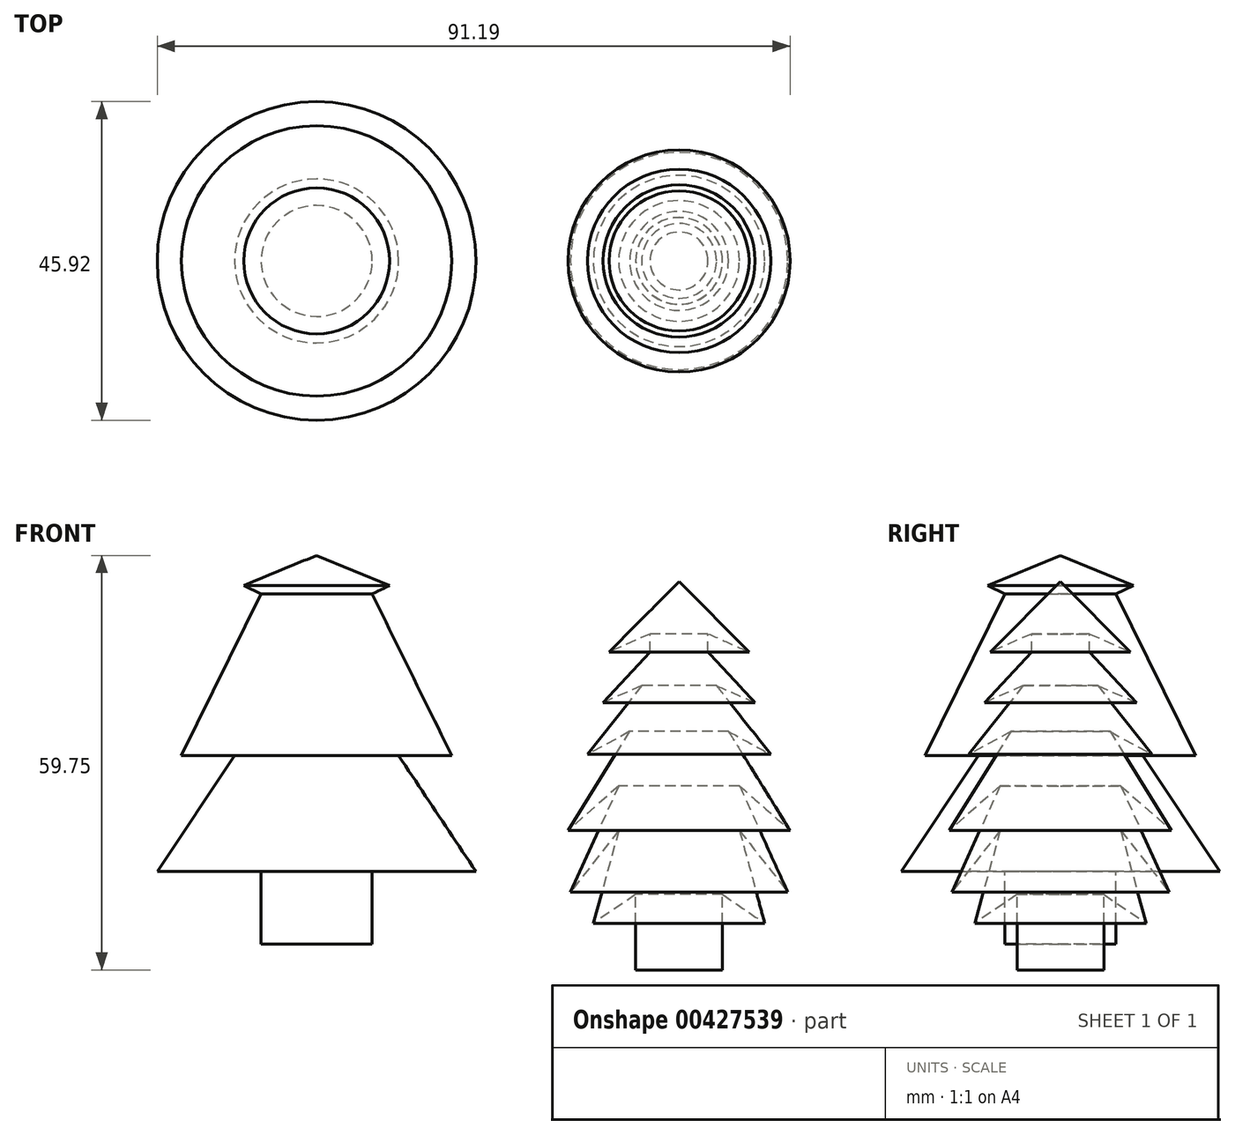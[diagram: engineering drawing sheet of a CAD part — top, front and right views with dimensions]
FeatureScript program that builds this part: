
annotation { "Feature Type Name" : "Feature", "Feature Type Description" : "" }
export const myFeature = defineFeature(function(context is Context, id is Id, definition is map)
    precondition{}
    {
        {
            var Q0;
            Q0=qCreatedBy(makeId("Front.planeOp"),FACE);
            var sketch = newSketch(context, id + "F0", { "sketchPlane" : qUnion([Q0])});
            skLineSegment(sketch, "E0", {"start": v(0, 29.44) * mm, "end": v(0, -21.36) * mm});
            skLineSegment(sketch, "E1", {"start": v(0, -21.36) * mm, "end": v(6.24, -21.36) * mm});
            skLineSegment(sketch, "E2", {"start": v(6.24, -21.36) * mm, "end": v(6.24, -26.54) * mm});
            skLineSegment(sketch, "E3", {"start": v(6.24, -26.54) * mm, "end": v(0, -26.54) * mm});
            skLineSegment(sketch, "E4", {"start": v(0, -26.54) * mm, "end": v(0, -21.36) * mm});
            skLineSegment(sketch, "E5", {"start": v(0, 29.44) * mm, "end": v(10.09, 19.3) * mm});
            skLineSegment(sketch, "E6", {"start": v(4.17, 19.3) * mm, "end": v(10.96, 12) * mm});
            skLineSegment(sketch, "E7", {"start": v(10.96, 12) * mm, "end": v(5.4, 14.44) * mm});
            skLineSegment(sketch, "E8", {"start": v(5.4, 14.44) * mm, "end": v(13.22, 4.52) * mm});
            skLineSegment(sketch, "E9", {"start": v(13.22, 4.52) * mm, "end": v(7.13, 7.83) * mm});
            skLineSegment(sketch, "E10", {"start": v(7.13, 7.83) * mm, "end": v(16, -6.44) * mm});
            skLineSegment(sketch, "E11", {"start": v(16, -6.44) * mm, "end": v(8.7, 0) * mm});
            skLineSegment(sketch, "E12", {"start": v(8.7, 0) * mm, "end": v(15.65, -15.3) * mm});
            skLineSegment(sketch, "E13", {"start": v(15.65, -15.3) * mm, "end": v(8.7, -6.44) * mm});
            skLineSegment(sketch, "E14", {"start": v(8.7, -6.44) * mm, "end": v(12.35, -19.83) * mm});
            skLineSegment(sketch, "E15", {"start": v(12.35, -19.83) * mm, "end": v(6.26, -15.65) * mm});
            skLineSegment(sketch, "E16", {"start": v(6.26, -15.65) * mm, "end": v(6.24, -21.36) * mm});
            skLineSegment(sketch, "E17", {"start": v(4.17, 19.3) * mm, "end": v(4.17, 21.92) * mm});
            skLineSegment(sketch, "E18", {"start": v(4.17, 21.92) * mm, "end": v(10.09, 19.3) * mm});
            skSolve(sketch);
        }
        {
            var Q0;
            Q0 = qSketchRegion(id + "F0", true);
            var Q1;
            Q1=sQuery(id+"F0.wireOp",EDGE,"E0");
            revolve(context, id + "F1", {"entities" : qUnion([Q0]), "axis" : qUnion([Q1]), "revolveType" : RevolveType.FULL});
        }
        {
            var Q0;
            Q0=qCreatedBy(makeId("Front.planeOp"),FACE);
            var sketch = newSketch(context, id + "F2", { "sketchPlane" : qUnion([Q0])});
            skLineSegment(sketch, "E19", {"start": v(-52.23, 42.95) * mm, "end": v(-52.23, -22.8) * mm});
            skLineSegment(sketch, "E20", {"start": v(-52.23, -22.8) * mm, "end": v(-44.23, -22.8) * mm});
            skLineSegment(sketch, "E21", {"start": v(-44.23, -22.8) * mm, "end": v(-44.23, -12.36) * mm});
            skLineSegment(sketch, "E22", {"start": v(-44.23, -12.36) * mm, "end": v(-29.27, -12.36) * mm});
            skLineSegment(sketch, "E23", {"start": v(-29.27, -12.36) * mm, "end": v(-40.4, 4.34) * mm});
            skLineSegment(sketch, "E24", {"start": v(-40.4, 4.34) * mm, "end": v(-32.75, 4.34) * mm});
            skLineSegment(sketch, "E25", {"start": v(-32.75, 4.34) * mm, "end": v(-44.23, 27.65) * mm});
            skLineSegment(sketch, "E26", {"start": v(-44.23, 27.65) * mm, "end": v(-41.72, 28.88) * mm});
            skLineSegment(sketch, "E27", {"start": v(-41.72, 28.88) * mm, "end": v(-52.23, 33.21) * mm});
            skSolve(sketch);
        }
        {
            var Q0;
            Q0 = qSketchRegion(id + "F2", true);
            var Q1;
            Q1=sQuery(id+"F2.wireOp",EDGE,"E19");
            revolve(context, id + "F3", {"entities" : qUnion([Q0]), "axis" : qUnion([Q1]), "revolveType" : RevolveType.FULL});
        }
    });
